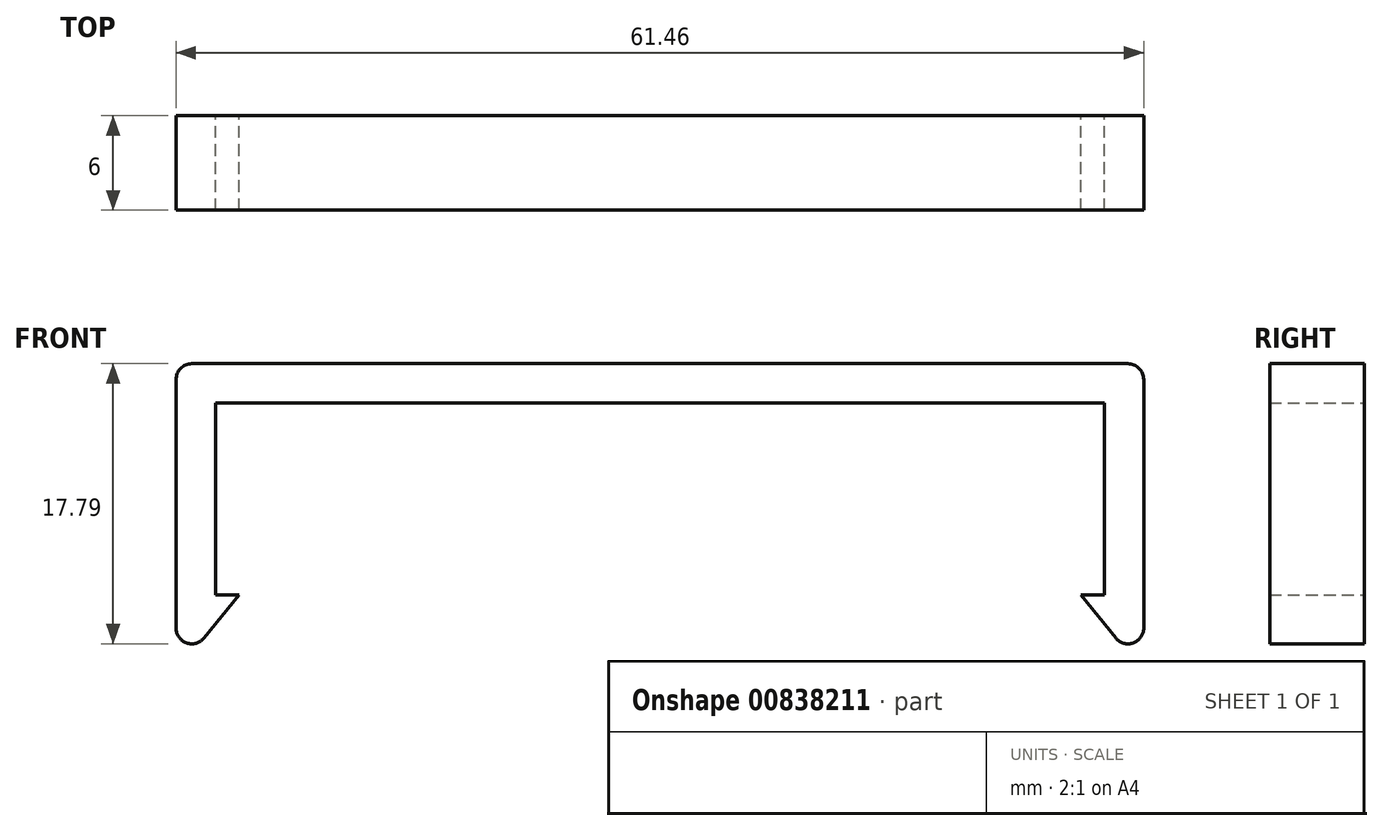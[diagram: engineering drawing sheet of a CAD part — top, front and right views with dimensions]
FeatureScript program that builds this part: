
annotation { "Feature Type Name" : "Feature", "Feature Type Description" : "" }
export const myFeature = defineFeature(function(context is Context, id is Id, definition is map)
    precondition{}
    {
        {
            var Q0;
            Q0=qCreatedBy(makeId("Front.planeOp"),FACE);
            var sketch = newSketch(context, id + "F0", { "sketchPlane" : qUnion([Q0])});
            skLineSegment(sketch, "E0.top", {"start": v(0, -12.2) * mm, "end": v(-1.5, -12.2) * mm});
            skLineSegment(sketch, "E0.left", {"start": v(0, 0) * mm, "end": v(0, -12.2) * mm, "construction": true});
            skLineSegment(sketch, "E1", {"start": v(2.5, -17.1) * mm, "end": v(2.5, 0) * mm});
            skLineSegment(sketch, "E2", {"start": v(0, 2.5) * mm, "end": v(-16.5, 2.5) * mm});
            skLineSegment(sketch, "E3", {"start": v(0, 0) * mm, "end": v(0, -12.2) * mm});
            skLineSegment(sketch, "E4", {"start": v(-10.1, 0) * mm, "end": v(0, 0) * mm});
            skLineSegment(sketch, "E5", {"start": v(0, 0) * mm, "end": v(0, 8.68) * mm, "construction": true});
            skLineSegment(sketch, "E6", {"start": v(0, -12.2) * mm, "end": v(0, -26.61) * mm, "construction": true});
            skPoint(sketch, "E7.orphan", {"position": v(-16.5, -14.7) * mm});
            skLineSegment(sketch, "E8", {"start": v(-1.5, -12.2) * mm, "end": v(2.5, -17.1) * mm});
            skLineSegment(sketch, "E9", {"start": v(2.5, 0) * mm, "end": v(2.5, 2.5) * mm});
            skLineSegment(sketch, "E10", {"start": v(2.5, 2.5) * mm, "end": v(0, 2.5) * mm});
            skLineSegment(sketch, "E11", {"start": v(-28.23, 8.15) * mm, "end": v(-28.23, -17.56) * mm, "construction": true});
            skLineSegment(sketch, "E12", {"start": v(-16.5, 2.5) * mm, "end": v(-28.23, 2.5) * mm});
            skLineSegment(sketch, "E13", {"start": v(-10.1, 0) * mm, "end": v(-28.23, 0) * mm});
            skLineSegment(sketch, "E14.MirrorCS", {"start": v(-39.96, 2.5) * mm, "end": v(-28.23, 2.5) * mm});
            skLineSegment(sketch, "E15.MirrorCS", {"start": v(-56.46, 2.5) * mm, "end": v(-39.96, 2.5) * mm});
            skLineSegment(sketch, "E16.MirrorCS", {"start": v(-46.36, 0) * mm, "end": v(-28.23, 0) * mm});
            skLineSegment(sketch, "E17.MirrorCS", {"start": v(-46.36, 0) * mm, "end": v(-56.46, 0) * mm});
            skLineSegment(sketch, "E18.MirrorCS", {"start": v(-58.96, 2.5) * mm, "end": v(-56.46, 2.5) * mm});
            skLineSegment(sketch, "E19.MirrorCS", {"start": v(-58.96, 0) * mm, "end": v(-58.96, 2.5) * mm});
            skLineSegment(sketch, "E20.MirrorCS", {"start": v(-58.96, -17.1) * mm, "end": v(-58.96, 0) * mm});
            skLineSegment(sketch, "E21.MirrorCS", {"start": v(-54.96, -12.2) * mm, "end": v(-58.96, -17.1) * mm});
            skLineSegment(sketch, "E22.MirrorCS", {"start": v(-56.46, -12.2) * mm, "end": v(-54.96, -12.2) * mm});
            skLineSegment(sketch, "E23.MirrorCS", {"start": v(-56.46, 0) * mm, "end": v(-56.46, -12.2) * mm, "construction": true});
            skLineSegment(sketch, "E24", {"start": v(-56.46, -12.2) * mm, "end": v(-56.46, 0) * mm});
            skSolve(sketch);
        }
        {
            var Q0;
            Q0 = qSketchRegion(id + "F0", true);
            extrude(context, id + "F1", {"entities" : qUnion([Q0]), "depth" : 6 * mm, "offsetDistance" : 25 * mm});
        }
        {
            var Q0;
            Q0=makeQuery(id+"F1.opExtrude","SWEPT_EDGE",EDGE,{"disambiguationData":[OSD([sQuery(id+"F0.wireOp",EDGE,"E20.MirrorCS"),sQuery(id+"F0.wireOp",EDGE,"E21.MirrorCS")])]});
            var Q1;
            Q1=makeQuery(id+"F1.opExtrude","SWEPT_EDGE",EDGE,{"disambiguationData":[OSD([sQuery(id+"F0.wireOp",EDGE,"E1"),sQuery(id+"F0.wireOp",EDGE,"E8")])]});
            var Q2;
            Q2=makeQuery(id+"F1.opExtrude","SWEPT_EDGE",EDGE,{"disambiguationData":[OSD([sQuery(id+"F0.wireOp",EDGE,"E18.MirrorCS"),sQuery(id+"F0.wireOp",EDGE,"E19.MirrorCS")])]});
            var Q3;
            Q3=makeQuery(id+"F1.opExtrude","SWEPT_EDGE",EDGE,{"disambiguationData":[OSD([sQuery(id+"F0.wireOp",EDGE,"E9"),sQuery(id+"F0.wireOp",EDGE,"E10")])]});
            fillet(context, id + "F2", {"entities" : qUnion([Q0, Q1, Q2, Q3]), "radius" : 1 * mm, "tangentPropagation" : true, "allowEdgeOverflow" : false});
        }
    });
